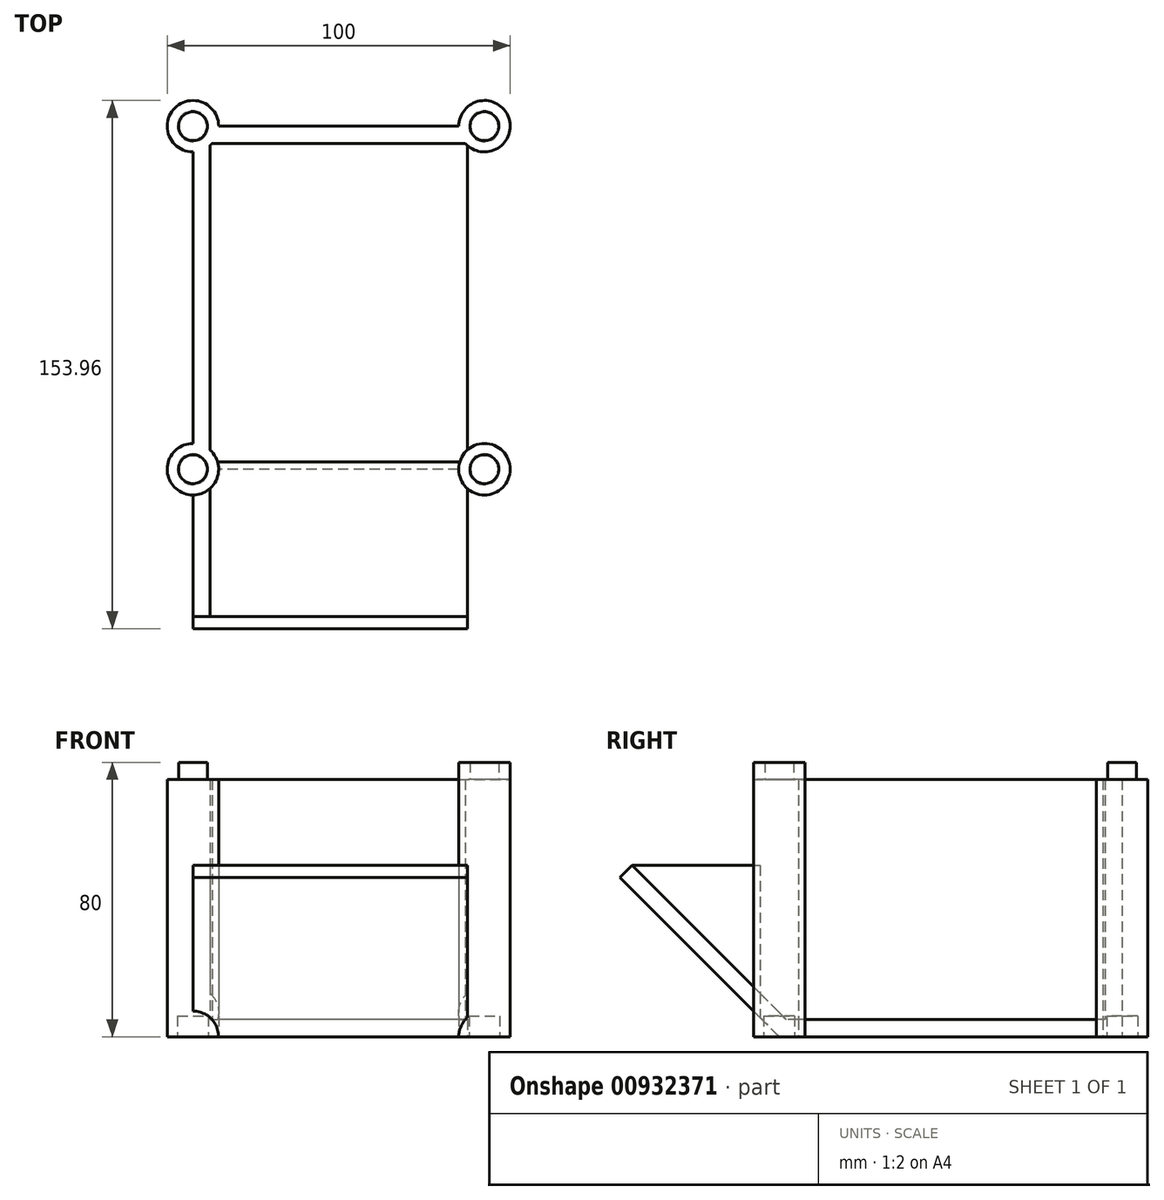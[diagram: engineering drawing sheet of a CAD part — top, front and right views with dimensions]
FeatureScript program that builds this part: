
annotation { "Feature Type Name" : "Feature", "Feature Type Description" : "" }
export const myFeature = defineFeature(function(context is Context, id is Id, definition is map)
    precondition{}
    {
        {
            assignVariable(context, id + "F0", {"name" : "depth", "anyValue" : 100});
        }
        {
            assignVariable(context, id + "F1", {"name" : "width", "anyValue" : 75});
        }
        {
            assignVariable(context, id + "F2", {"name" : "wall", "anyValue" : 5});
        }
        {
            var Q0;
            Q0=qCreatedBy(makeId("Right.planeOp"),FACE);
            var sketch = newSketch(context, id + "F3", { "sketchPlane" : qUnion([Q0])});
            skLineSegment(sketch, "E0", {"start": v(50, 0) * mm, "end": v(-50, 0) * mm});
            skLineSegment(sketch, "E1", {"start": v(-50, 0) * mm, "end": v(-96.46, 46.46) * mm});
            skLineSegment(sketch, "E2", {"start": v(-96.46, 46.46) * mm, "end": v(-92.93, 50) * mm});
            skLineSegment(sketch, "E3", {"start": v(-92.93, 50) * mm, "end": v(-47.93, 5) * mm});
            skLineSegment(sketch, "E4", {"start": v(50, 50) * mm, "end": v(50, 0) * mm});
            skLineSegment(sketch, "E5", {"start": v(-47.93, 5) * mm, "end": v(-50, 0) * mm, "construction": true});
            skLineSegment(sketch, "E6", {"start": v(45, 5) * mm, "end": v(-47.93, 5) * mm});
            skLineSegment(sketch, "E7", {"start": v(45, 5) * mm, "end": v(45, 50) * mm});
            skLineSegment(sketch, "E8", {"start": v(45, 50) * mm, "end": v(50, 50) * mm});
            skLineSegment(sketch, "E9", {"start": v(45, 50) * mm, "end": v(-92.93, 50) * mm, "construction": true});
            skSolve(sketch);
        }
        {
            var Q0;
            Q0=makeQuery(id+"F3.imprint","IMPRINT",FACE,{"disambiguationData":[TD([[makeQuery(id+"F3.imprint","IMPRINT",EDGE,{"derivedFrom":sQuery(id+"F3.wireOp",EDGE,"E0")}),-1.0]])]});
            extrude(context, id + "F4", {"entities" : qUnion([Q0]), "endBound" : BoundingType.SYMMETRIC, "depth" : (getVariable(context, 'width')) * mm, "offsetDistance" : 25 * mm});
        }
        {
            var Q0;
            Q0=makeQuery(id+"F4.opExtrude","CAP_FACE",FACE,{"disambiguationData":[OSD([sQuery(id+"F3.wireOp",EDGE,"E0"),sQuery(id+"F3.wireOp",EDGE,"E1"),sQuery(id+"F3.wireOp",EDGE,"E2"),sQuery(id+"F3.wireOp",EDGE,"E3"),sQuery(id+"F3.wireOp",EDGE,"E4"),sQuery(id+"F3.wireOp",EDGE,"E6"),sQuery(id+"F3.wireOp",EDGE,"E7"),sQuery(id+"F3.wireOp",EDGE,"E8")])],"isStart":true});
            var sketch = newSketch(context, id + "F5", { "sketchPlane" : qUnion([Q0])});
            skLineSegment(sketch, "E10", {"start": v(92.93, 50) * mm, "end": v(-45, 50) * mm});
            skSolve(sketch);
        }
        {
            var Q0;
            {var subQ0=sQuery(id+"F5.wireOp",EDGE,"E10");Q0=makeQuery(id+"F5.imprint","IMPRINT",FACE,{"disambiguationData":[TD([[makeQuery(id+"F5.imprint","IMPRINT",EDGE,{"derivedFrom":subQ0}),1.0]])]});}
            var Q1;
            Q1=makeQuery(id+"F5.imprint","IMPRINT",FACE,{"disambiguationData":[TD([[makeQuery(id+"F5.imprint","IMPRINT",EDGE,{"derivedFrom":makeQuery(id+"F4.opExtrude","CAP_EDGE",EDGE,{"disambiguationData":[OSD([sQuery(id+"F3.wireOp",EDGE,"E0")])],"isStart":true})}),1.0]])]});
            extrude(context, id + "F6", {"entities" : qUnion([Q0, Q1]), "operationType" : NewBodyOperationType.ADD, "depth" : (getVariable(context, 'wall')) * mm, "offsetDistance" : 25 * mm});
        }
        {
            var Q0;
            {var subQ0=sQuery(id+"F3.wireOp",EDGE,"E0");Q0=makeQuery(id+"FtaCGZXW4uEEXou_1.1.F6.boolean.opBoolean","MERGE",FACE,{"derivedFrom":[makeQuery(id+"F6.boolean.opBoolean","MERGE",FACE,{"derivedFrom":[makeQuery(id+"F4.opExtrude","SWEPT_FACE",FACE,{"disambiguationData":[OSD([subQ0])]}),makeQuery(id+"F6.opExtrude","SWEPT_FACE",FACE,{"disambiguationData":[OSD([subQ0])]})]}),makeQuery(id+"FtaCGZXW4uEEXou_1.1.F6.opExtrude","SWEPT_FACE",FACE,{"disambiguationData":[OSD([subQ0])]})]});}
            var sketch = newSketch(context, id + "F7", { "sketchPlane" : qUnion([Q0])});
            skCircle(sketch, "E11", {"center": v(-42.5, -50) * mm, "radius": 7.5 * mm});
            skCircle(sketch, "E12", {"center": v(42.5, -50) * mm, "radius": 7.5 * mm});
            skCircle(sketch, "E13", {"center": v(42.5, 50) * mm, "radius": 7.5 * mm});
            skCircle(sketch, "E14", {"center": v(-42.5, 50) * mm, "radius": 7.5 * mm});
            skSolve(sketch);
        }
        {
            var Q0;
            Q0 = qSketchRegion(id + "F7", true);
            extrude(context, id + "F8", {"entities" : qUnion([Q0]), "operationType" : NewBodyOperationType.ADD, "oppositeDirection" : true, "depth" : (getVariable(context, 'depth') * .75) * mm, "offsetDistance" : 25 * mm});
        }
        {
            var Q0;
            {var subQ0=sQuery(id+"F3.wireOp",EDGE,"E0");Q0=makeQuery(id+"F8.boolean.opBoolean","MERGE",FACE,{"derivedFrom":[makeQuery(id+"FtaCGZXW4uEEXou_1.1.F6.boolean.opBoolean","MERGE",FACE,{"derivedFrom":[makeQuery(id+"F6.boolean.opBoolean","MERGE",FACE,{"derivedFrom":[makeQuery(id+"F4.opExtrude","SWEPT_FACE",FACE,{"disambiguationData":[OSD([subQ0])]}),makeQuery(id+"F6.opExtrude","SWEPT_FACE",FACE,{"disambiguationData":[OSD([subQ0])]})]}),makeQuery(id+"FtaCGZXW4uEEXou_1.1.F6.opExtrude","SWEPT_FACE",FACE,{"disambiguationData":[OSD([subQ0])]})]}),makeQuery(id+"F8.opExtrude","CAP_FACE",FACE,{"disambiguationData":[OSD([sQuery(id+"F7.wireOp",EDGE,"E11")])],"isStart":true}),makeQuery(id+"F8.opExtrude","CAP_FACE",FACE,{"disambiguationData":[OSD([sQuery(id+"F7.wireOp",EDGE,"E12")])],"isStart":true}),makeQuery(id+"F8.opExtrude","CAP_FACE",FACE,{"disambiguationData":[OSD([sQuery(id+"F7.wireOp",EDGE,"E13")])],"isStart":true}),makeQuery(id+"F8.opExtrude","CAP_FACE",FACE,{"disambiguationData":[OSD([sQuery(id+"F7.wireOp",EDGE,"E14")])],"isStart":true})]});}
            var sketch = newSketch(context, id + "F9", { "sketchPlane" : qUnion([Q0])});
            skArc(sketch, "E15.0", {"start": v(-42.5, -42.5) * mm, "mid": v(-47.8, -55.3) * mm, "end": v(-35, -50) * mm, "construction": true});
            skArc(sketch, "E16.0", {"start": v(-35, 50) * mm, "mid": v(-47.8, 55.3) * mm, "end": v(-42.5, 42.5) * mm, "construction": true});
            skArc(sketch, "E17.0", {"start": v(35, -50) * mm, "mid": v(47.8, -55.3) * mm, "end": v(42.5, -42.5) * mm, "construction": true});
            skArc(sketch, "E18.0", {"start": v(42.5, 42.5) * mm, "mid": v(47.8, 55.3) * mm, "end": v(35, 50) * mm, "construction": true});
            skCircle(sketch, "E19", {"center": v(-42.5, -50) * mm, "radius": 4.5 * mm});
            skCircle(sketch, "E20", {"center": v(-42.5, 50) * mm, "radius": 4.5 * mm});
            skCircle(sketch, "E21", {"center": v(42.5, -50) * mm, "radius": 4.5 * mm});
            skCircle(sketch, "E22", {"center": v(42.5, 50) * mm, "radius": 4.5 * mm});
            skSolve(sketch);
        }
        {
            var Q0;
            Q0=makeQuery(id+"F9.imprint","IMPRINT",FACE,{"disambiguationData":[TD([[makeQuery(id+"F9.imprint","IMPRINT",EDGE,{"derivedFrom":sQuery(id+"F9.wireOp",EDGE,"E19")}),1.0]])]});
            var Q1;
            Q1=makeQuery(id+"F9.imprint","IMPRINT",FACE,{"disambiguationData":[TD([[makeQuery(id+"F9.imprint","IMPRINT",EDGE,{"derivedFrom":sQuery(id+"F9.wireOp",EDGE,"E20")}),1.0]])]});
            var Q2;
            Q2=makeQuery(id+"F9.imprint","IMPRINT",FACE,{"disambiguationData":[TD([[makeQuery(id+"F9.imprint","IMPRINT",EDGE,{"derivedFrom":sQuery(id+"F9.wireOp",EDGE,"E22")}),1.0]])]});
            var Q3;
            Q3=makeQuery(id+"F9.imprint","IMPRINT",FACE,{"disambiguationData":[TD([[makeQuery(id+"F9.imprint","IMPRINT",EDGE,{"derivedFrom":sQuery(id+"F9.wireOp",EDGE,"E21")}),1.0]])]});
            extrude(context, id + "F10", {"entities" : qUnion([Q0, Q1, Q2, Q3]), "operationType" : NewBodyOperationType.REMOVE, "oppositeDirection" : true, "depth" : 6 * mm, "offsetDistance" : 25 * mm});
        }
        {
            var Q0;
            Q0=makeQuery(id+"F8.opExtrude","CAP_FACE",FACE,{"disambiguationData":[OSD([sQuery(id+"F7.wireOp",EDGE,"E13")])],"isStart":false});
            var sketch = newSketch(context, id + "F11", { "sketchPlane" : qUnion([Q0])});
            skCircle(sketch, "E23.0", {"center": v(42.5, -50) * mm, "radius": 4.2 * mm});
            skCircle(sketch, "E24.0.0", {"center": v(-42.5, 50) * mm, "radius": 7.5 * mm, "construction": true});
            skCircle(sketch, "E25.0.0", {"center": v(42.5, 50) * mm, "radius": 7.5 * mm, "construction": true});
            skCircle(sketch, "E26.0.0", {"center": v(-42.5, -50) * mm, "radius": 7.5 * mm, "construction": true});
            skCircle(sketch, "E27", {"center": v(-42.5, -50) * mm, "radius": 4.2 * mm});
            skCircle(sketch, "E28", {"center": v(-42.5, 50) * mm, "radius": 4.2 * mm});
            skCircle(sketch, "E29", {"center": v(42.5, 50) * mm, "radius": 4.2 * mm});
            skSolve(sketch);
        }
        {
            var Q0;
            Q0=makeQuery(id+"F11.imprint","IMPRINT",FACE,{"disambiguationData":[TD([[makeQuery(id+"F11.imprint","IMPRINT",EDGE,{"derivedFrom":sQuery(id+"F11.wireOp",EDGE,"E29")}),1.0]])]});
            var Q1;
            Q1=makeQuery(id+"F11.imprint","IMPRINT",FACE,{"disambiguationData":[TD([[makeQuery(id+"F11.imprint","IMPRINT",EDGE,{"derivedFrom":sQuery(id+"F11.wireOp",EDGE,"E28")}),1.0]])]});
            var Q2;
            Q2=makeQuery(id+"F11.imprint","IMPRINT",FACE,{"disambiguationData":[TD([[makeQuery(id+"F11.imprint","IMPRINT",EDGE,{"derivedFrom":sQuery(id+"F11.wireOp",EDGE,"E27")}),1.0]])]});
            var Q3;
            Q3=makeQuery(id+"F11.imprint","IMPRINT",FACE,{"disambiguationData":[TD([[makeQuery(id+"F11.imprint","IMPRINT",EDGE,{"derivedFrom":sQuery(id+"F11.wireOp",EDGE,"E23.0")}),-1.0]])]});
            extrude(context, id + "F12", {"entities" : qUnion([Q0, Q1, Q2, Q3]), "operationType" : NewBodyOperationType.ADD, "depth" : 5 * mm, "offsetDistance" : 25 * mm});
        }
        {
            var Q0;
            {var subQ0=sQuery(id+"F5.wireOp",EDGE,"E10");var subQ1=sQuery(id+"F3.wireOp",EDGE,"E8");var subQ2=sQuery(id+"F3.wireOp",EDGE,"E4");var subQ3=sQuery(id+"F3.wireOp",EDGE,"E2");var subQ4=sQuery(id+"F3.wireOp",EDGE,"E1");var subQ5=sQuery(id+"F3.wireOp",EDGE,"E0");Q0=makeQuery(id+"F8.boolean.opBoolean","SPLIT",FACE,{"disambiguationData":[TD([makeQuery(id+"F6.opExtrude","CAP_FACE",FACE,{"disambiguationData":[OSD([subQ5,subQ4,subQ3,subQ2,subQ1,subQ0])],"isStart":true}),makeQuery(id+"F6.opExtrude","CAP_FACE",FACE,{"disambiguationData":[OSD([subQ5,subQ4,subQ3,subQ2,subQ1,subQ0])],"isStart":false}),makeQuery(id+"F8.opExtrude","SWEPT_FACE",FACE,{"disambiguationData":[OSD([sQuery(id+"F7.wireOp",EDGE,"E11")])]}),makeQuery(id+"F8.opExtrude","SWEPT_FACE",FACE,{"disambiguationData":[OSD([sQuery(id+"F7.wireOp",EDGE,"E14")])]})])],"derivedFrom":makeQuery(id+"FtaCGZXW4uEEXou_1.1.F6.boolean.opBoolean","MERGE",FACE,{"derivedFrom":[makeQuery(id+"F6.boolean.opBoolean","MERGE",FACE,{"derivedFrom":[makeQuery(id+"F4.opExtrude","SWEPT_FACE",FACE,{"disambiguationData":[OSD([subQ1])]}),makeQuery(id+"F6.opExtrude","SWEPT_FACE",FACE,{"disambiguationData":[OSD([subQ1,subQ0])]})]}),makeQuery(id+"FtaCGZXW4uEEXou_1.1.F6.opExtrude","SWEPT_FACE",FACE,{"disambiguationData":[OSD([subQ1,subQ0])]})]})});}
            var Q1;
            {var subQ0=sQuery(id+"F3.wireOp",EDGE,"E4");var subQ1=sQuery(id+"F5.wireOp",EDGE,"E10");var subQ2=sQuery(id+"F3.wireOp",EDGE,"E8");Q1=makeQuery(id+"F8.boolean.opBoolean","SPLIT",FACE,{"disambiguationData":[TD([makeQuery(id+"F4.opExtrude","SWEPT_FACE",FACE,{"disambiguationData":[OSD([subQ0])]}),makeQuery(id+"F4.opExtrude","SWEPT_FACE",FACE,{"disambiguationData":[OSD([sQuery(id+"F3.wireOp",EDGE,"E7")])]}),makeQuery(id+"F6.opExtrude","SWEPT_FACE",FACE,{"disambiguationData":[OSD([subQ0])]}),makeQuery(id+"FtaCGZXW4uEEXou_1.1.F6.opExtrude","SWEPT_FACE",FACE,{"disambiguationData":[OSD([subQ0])]}),makeQuery(id+"F8.opExtrude","SWEPT_FACE",FACE,{"disambiguationData":[OSD([sQuery(id+"F7.wireOp",EDGE,"E11")])]}),makeQuery(id+"F8.opExtrude","SWEPT_FACE",FACE,{"disambiguationData":[OSD([sQuery(id+"F7.wireOp",EDGE,"E12")])]})])],"derivedFrom":makeQuery(id+"FtaCGZXW4uEEXou_1.1.F6.boolean.opBoolean","MERGE",FACE,{"derivedFrom":[makeQuery(id+"F6.boolean.opBoolean","MERGE",FACE,{"derivedFrom":[makeQuery(id+"F4.opExtrude","SWEPT_FACE",FACE,{"disambiguationData":[OSD([subQ2])]}),makeQuery(id+"F6.opExtrude","SWEPT_FACE",FACE,{"disambiguationData":[OSD([subQ2,subQ1])]})]}),makeQuery(id+"FtaCGZXW4uEEXou_1.1.F6.opExtrude","SWEPT_FACE",FACE,{"disambiguationData":[OSD([subQ2,subQ1])]})]})});}
            var Q2;
            {var subQ0=sQuery(id+"F5.wireOp",EDGE,"E10");var subQ1=sQuery(id+"F3.wireOp",EDGE,"E8");var subQ2=sQuery(id+"F3.wireOp",EDGE,"E4");var subQ3=sQuery(id+"F3.wireOp",EDGE,"E2");var subQ4=sQuery(id+"F3.wireOp",EDGE,"E1");var subQ5=sQuery(id+"F3.wireOp",EDGE,"E0");Q2=makeQuery(id+"F8.boolean.opBoolean","SPLIT",FACE,{"disambiguationData":[TD([makeQuery(id+"FtaCGZXW4uEEXou_1.1.F6.opExtrude","CAP_FACE",FACE,{"disambiguationData":[OSD([subQ5,subQ4,subQ3,subQ2,subQ1,subQ0])],"isStart":true}),makeQuery(id+"FtaCGZXW4uEEXou_1.1.F6.opExtrude","CAP_FACE",FACE,{"disambiguationData":[OSD([subQ5,subQ4,subQ3,subQ2,subQ1,subQ0])],"isStart":false}),makeQuery(id+"F8.opExtrude","SWEPT_FACE",FACE,{"disambiguationData":[OSD([sQuery(id+"F7.wireOp",EDGE,"E12")])]}),makeQuery(id+"F8.opExtrude","SWEPT_FACE",FACE,{"disambiguationData":[OSD([sQuery(id+"F7.wireOp",EDGE,"E13")])]})])],"derivedFrom":makeQuery(id+"FtaCGZXW4uEEXou_1.1.F6.boolean.opBoolean","MERGE",FACE,{"derivedFrom":[makeQuery(id+"F6.boolean.opBoolean","MERGE",FACE,{"derivedFrom":[makeQuery(id+"F4.opExtrude","SWEPT_FACE",FACE,{"disambiguationData":[OSD([subQ1])]}),makeQuery(id+"F6.opExtrude","SWEPT_FACE",FACE,{"disambiguationData":[OSD([subQ1,subQ0])]})]}),makeQuery(id+"FtaCGZXW4uEEXou_1.1.F6.opExtrude","SWEPT_FACE",FACE,{"disambiguationData":[OSD([subQ1,subQ0])]})]})});}
            var Q3;
            Q3=makeQuery(id+"F8.opExtrude","CAP_FACE",FACE,{"disambiguationData":[OSD([sQuery(id+"F7.wireOp",EDGE,"E11")])],"isStart":false});
            extrude(context, id + "F13", {"entities" : qUnion([Q0, Q1, Q2]), "operationType" : NewBodyOperationType.ADD, "endBound" : BoundingType.UP_TO_SURFACE, "depth" : 25 * mm, "endBoundEntityFace" : qUnion([Q3]), "offsetDistance" : 25 * mm});
        }
    });
